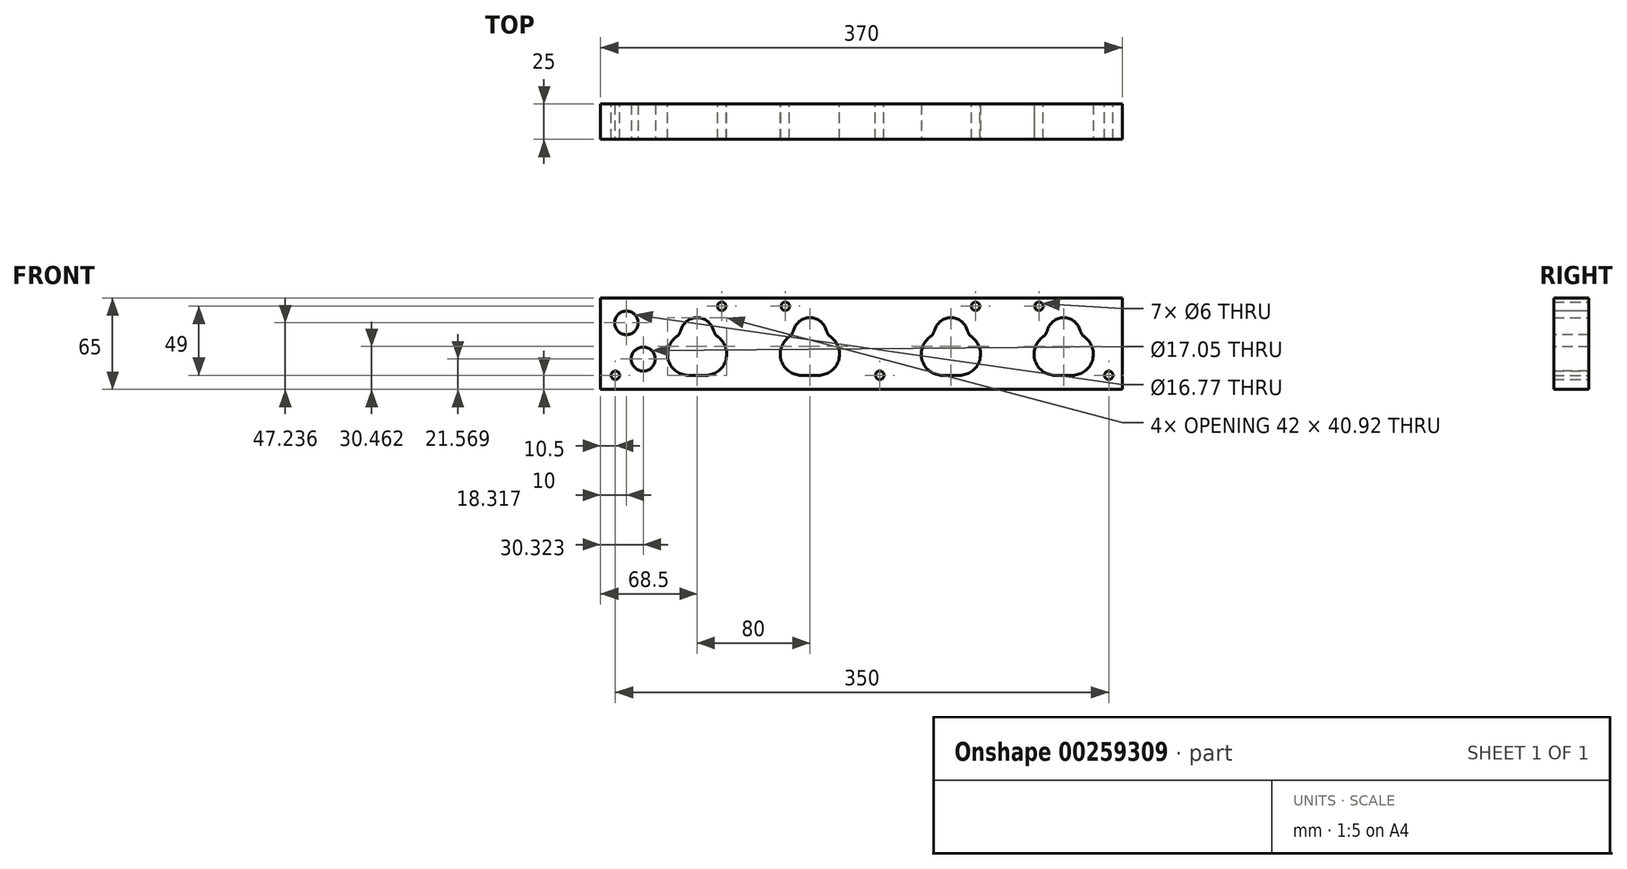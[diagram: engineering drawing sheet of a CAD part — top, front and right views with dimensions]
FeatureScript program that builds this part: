
annotation { "Feature Type Name" : "Feature", "Feature Type Description" : "" }
export const myFeature = defineFeature(function(context is Context, id is Id, definition is map)
    precondition{}
    {
        {
            var Q0;
            Q0=qCreatedBy(makeId("Front.planeOp"),FACE);
            var sketch = newSketch(context, id + "F0", { "sketchPlane" : qUnion([Q0])});
            skCircle(sketch, "E0", {"center": v(-174.5, -22.5) * mm, "radius": 3 * mm});
            skCircle(sketch, "E1", {"center": v(13, -22.5) * mm, "radius": 3 * mm});
            skCircle(sketch, "E2", {"center": v(175.5, -22.5) * mm, "radius": 3 * mm});
            skCircle(sketch, "E3", {"center": v(-99, 26.5) * mm, "radius": 3 * mm});
            skCircle(sketch, "E4", {"center": v(-54, 26.5) * mm, "radius": 3 * mm});
            skCircle(sketch, "E5", {"center": v(81, 26.5) * mm, "radius": 3 * mm});
            skCircle(sketch, "E6", {"center": v(126, 26.5) * mm, "radius": 3 * mm});
            skLineSegment(sketch, "E7.bottom", {"start": v(-185, 32.5) * mm, "end": v(185, 32.5) * mm});
            skLineSegment(sketch, "E7.top", {"start": v(-185, -32.5) * mm, "end": v(185, -32.5) * mm});
            skLineSegment(sketch, "E7.left", {"start": v(-185, 32.5) * mm, "end": v(-185, -32.5) * mm});
            skLineSegment(sketch, "E7.right", {"start": v(185, 32.5) * mm, "end": v(185, -32.5) * mm});
            skPoint(sketch, "E7.middle", {"position": v(0, 0) * mm});
            skArc(sketch, "E8", {"start": v(-104.95, 9.66) * mm, "mid": v(-116.5, 18.42) * mm, "end": v(-128.05, 9.66) * mm});
            skArc(sketch, "E9", {"start": v(-131.61, 4.42) * mm, "mid": v(-136.7, -12.3) * mm, "end": v(-122.5, -22.5) * mm});
            skArc(sketch, "E10", {"start": v(-110.5, -22.5) * mm, "mid": v(-96.3, -12.3) * mm, "end": v(-101.39, 4.42) * mm});
            skLineSegment(sketch, "E11", {"start": v(-122.5, -22.5) * mm, "end": v(-110.5, -22.5) * mm});
            skPoint(sketch, "E12.visualSharp", {"position": v(-128.5, 6.25) * mm});
            skArc(sketch, "E12.filletArc", {"start": v(-131.61, 4.42) * mm, "mid": v(-129.4, 6.75) * mm, "end": v(-128.05, 9.66) * mm});
            skPoint(sketch, "E13.visualSharp", {"position": v(-104.5, 6.25) * mm});
            skArc(sketch, "E13.filletArc", {"start": v(-104.95, 9.66) * mm, "mid": v(-103.6, 6.75) * mm, "end": v(-101.39, 4.42) * mm});
            skArc(sketch, "E14.1.0.0", {"start": v(-24.95, 9.66) * mm, "mid": v(-36.5, 18.42) * mm, "end": v(-48.05, 9.66) * mm});
            skArc(sketch, "E14.1.0.1", {"start": v(-51.61, 4.42) * mm, "mid": v(-49.4, 6.75) * mm, "end": v(-48.05, 9.66) * mm});
            skArc(sketch, "E14.1.0.2", {"start": v(-51.61, 4.42) * mm, "mid": v(-56.7, -12.3) * mm, "end": v(-42.5, -22.5) * mm});
            skLineSegment(sketch, "E14.1.0.3", {"start": v(-42.5, -22.5) * mm, "end": v(-30.5, -22.5) * mm});
            skArc(sketch, "E14.1.0.4", {"start": v(-30.5, -22.5) * mm, "mid": v(-16.3, -12.3) * mm, "end": v(-21.39, 4.42) * mm});
            skArc(sketch, "E14.1.0.5", {"start": v(-24.95, 9.66) * mm, "mid": v(-23.6, 6.75) * mm, "end": v(-21.39, 4.42) * mm});
            skLineSegment(sketch, "E14.direction1", {"start": v(-128.05, 9.66) * mm, "end": v(-48.05, 9.66) * mm, "construction": true});
            skSolve(sketch);
        }
        {
            var Q0;
            Q0=makeQuery(id+"F0.imprint","IMPRINT",FACE,{"disambiguationData":[TD([[makeQuery(id+"F0.imprint","IMPRINT",EDGE,{"derivedFrom":sQuery(id+"F0.wireOp",EDGE,"E0")}),-1.0]])]});
            extrude(context, id + "F1", {"entities" : qUnion([Q0]), "depth" : 25 * mm});
        }
        {
            var Q0;
            Q0=makeQuery(id+"F1.opExtrude","CAP_FACE",FACE,{"disambiguationData":[OSD([sQuery(id+"F0.wireOp",EDGE,"E0"),sQuery(id+"F0.wireOp",EDGE,"E1"),sQuery(id+"F0.wireOp",EDGE,"E2"),sQuery(id+"F0.wireOp",EDGE,"E3"),sQuery(id+"F0.wireOp",EDGE,"E4"),sQuery(id+"F0.wireOp",EDGE,"E5"),sQuery(id+"F0.wireOp",EDGE,"E6"),sQuery(id+"F0.wireOp",EDGE,"E7.bottom"),sQuery(id+"F0.wireOp",EDGE,"E7.top"),sQuery(id+"F0.wireOp",EDGE,"E7.left"),sQuery(id+"F0.wireOp",EDGE,"E7.right"),sQuery(id+"F0.wireOp",EDGE,"E8"),sQuery(id+"F0.wireOp",EDGE,"E9"),sQuery(id+"F0.wireOp",EDGE,"E10"),sQuery(id+"F0.wireOp",EDGE,"E11"),sQuery(id+"F0.wireOp",EDGE,"E12.filletArc"),sQuery(id+"F0.wireOp",EDGE,"E13.filletArc"),sQuery(id+"F0.wireOp",EDGE,"E14.1.0.0"),sQuery(id+"F0.wireOp",EDGE,"E14.1.0.1"),sQuery(id+"F0.wireOp",EDGE,"E14.1.0.2"),sQuery(id+"F0.wireOp",EDGE,"E14.1.0.3"),sQuery(id+"F0.wireOp",EDGE,"E14.1.0.4"),sQuery(id+"F0.wireOp",EDGE,"E14.1.0.5")])],"isStart":false});
            var sketch = newSketch(context, id + "F2", { "sketchPlane" : qUnion([Q0])});
            skArc(sketch, "E15.0", {"start": v(69.5, -22.5) * mm, "mid": v(83.7, -12.3) * mm, "end": v(78.61, 4.42) * mm});
            skArc(sketch, "E15.1", {"start": v(75.05, 9.66) * mm, "mid": v(76.4, 6.75) * mm, "end": v(78.61, 4.42) * mm});
            skArc(sketch, "E15.2", {"start": v(75.05, 9.66) * mm, "mid": v(63.5, 18.42) * mm, "end": v(51.95, 9.66) * mm});
            skArc(sketch, "E15.3", {"start": v(48.39, 4.42) * mm, "mid": v(50.6, 6.75) * mm, "end": v(51.95, 9.66) * mm});
            skArc(sketch, "E15.4", {"start": v(48.39, 4.42) * mm, "mid": v(43.3, -12.3) * mm, "end": v(57.5, -22.5) * mm});
            skLineSegment(sketch, "E15.5", {"start": v(137.5, -22.5) * mm, "end": v(149.5, -22.5) * mm});
            skArc(sketch, "E15.6", {"start": v(128.39, 4.42) * mm, "mid": v(123.3, -12.3) * mm, "end": v(137.5, -22.5) * mm});
            skArc(sketch, "E15.7", {"start": v(128.39, 4.42) * mm, "mid": v(130.6, 6.75) * mm, "end": v(131.95, 9.66) * mm});
            skArc(sketch, "E15.8", {"start": v(155.05, 9.66) * mm, "mid": v(143.5, 18.42) * mm, "end": v(131.95, 9.66) * mm});
            skArc(sketch, "E15.9", {"start": v(155.05, 9.66) * mm, "mid": v(156.4, 6.75) * mm, "end": v(158.61, 4.42) * mm});
            skArc(sketch, "E15.10", {"start": v(149.5, -22.5) * mm, "mid": v(163.7, -12.3) * mm, "end": v(158.61, 4.42) * mm});
            skCircle(sketch, "E15.11", {"center": v(126, 26.5) * mm, "radius": 3 * mm});
            skCircle(sketch, "E15.12", {"center": v(81, 26.5) * mm, "radius": 3 * mm});
            skLineSegment(sketch, "E15.13", {"start": v(57.5, -22.5) * mm, "end": v(69.5, -22.5) * mm});
            skSolve(sketch);
        }
        {
            var Q0;
            Q0=makeQuery(id+"F2.imprint","IMPRINT",FACE,{"disambiguationData":[TD([[makeQuery(id+"F2.imprint","IMPRINT",EDGE,{"derivedFrom":sQuery(id+"F2.wireOp",EDGE,"E15.5")}),1.0]])]});
            var Q1;
            Q1=makeQuery(id+"F2.imprint","IMPRINT",FACE,{"disambiguationData":[TD([[makeQuery(id+"F2.imprint","IMPRINT",EDGE,{"derivedFrom":sQuery(id+"F2.wireOp",EDGE,"E15.0")}),1.0]])]});
            extrude(context, id + "F3", {"entities" : qUnion([Q0, Q1]), "operationType" : NewBodyOperationType.REMOVE, "oppositeDirection" : true, "depth" : 25 * mm});
        }
        {
            var Q0;
            Q0=makeQuery(id+"F1.opExtrude","CAP_FACE",FACE,{"disambiguationData":[OSD([sQuery(id+"F0.wireOp",EDGE,"E0"),sQuery(id+"F0.wireOp",EDGE,"E1"),sQuery(id+"F0.wireOp",EDGE,"E2"),sQuery(id+"F0.wireOp",EDGE,"E3"),sQuery(id+"F0.wireOp",EDGE,"E4"),sQuery(id+"F0.wireOp",EDGE,"E5"),sQuery(id+"F0.wireOp",EDGE,"E6"),sQuery(id+"F0.wireOp",EDGE,"E7.bottom"),sQuery(id+"F0.wireOp",EDGE,"E7.top"),sQuery(id+"F0.wireOp",EDGE,"E7.left"),sQuery(id+"F0.wireOp",EDGE,"E7.right"),sQuery(id+"F0.wireOp",EDGE,"E8"),sQuery(id+"F0.wireOp",EDGE,"E9"),sQuery(id+"F0.wireOp",EDGE,"E10"),sQuery(id+"F0.wireOp",EDGE,"E11"),sQuery(id+"F0.wireOp",EDGE,"E12.filletArc"),sQuery(id+"F0.wireOp",EDGE,"E13.filletArc"),sQuery(id+"F0.wireOp",EDGE,"E14.1.0.0"),sQuery(id+"F0.wireOp",EDGE,"E14.1.0.1"),sQuery(id+"F0.wireOp",EDGE,"E14.1.0.2"),sQuery(id+"F0.wireOp",EDGE,"E14.1.0.3"),sQuery(id+"F0.wireOp",EDGE,"E14.1.0.4"),sQuery(id+"F0.wireOp",EDGE,"E14.1.0.5")])],"isStart":false});
            var sketch = newSketch(context, id + "F4", { "sketchPlane" : qUnion([Q0])});
            skCircle(sketch, "E16", {"center": v(-166.68, 14.74) * mm, "radius": 8.38 * mm});
            skCircle(sketch, "E17", {"center": v(-154.68, -10.93) * mm, "radius": 8.52 * mm});
            skSolve(sketch);
        }
        {
            var Q0;
            Q0 = qSketchRegion(id + "F4", true);
            extrude(context, id + "F5", {"entities" : qUnion([Q0]), "operationType" : NewBodyOperationType.REMOVE, "oppositeDirection" : true, "depth" : 25 * mm});
        }
    });
